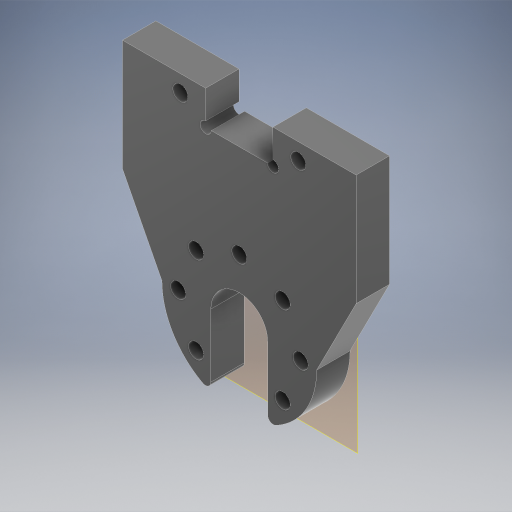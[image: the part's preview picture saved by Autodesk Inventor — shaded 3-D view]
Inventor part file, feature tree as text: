
AUTODESK INVENTOR PART (.ipt)
format: ipt  version: 2024 (Build 280153000, 153)  size: 315,904 bytes
history: native  units: in
note: dims shown in document units (in); Inventor stores cm internally (conversion verified against a paired STEP export)
features: other x3, extrude x2, sketch x2, fillet x1, reference x1
ambient origin geometry x8: Origin, YZ Plane, XZ Plane, XY Plane, X Axis, Y Axis, Z Axis, Center Point
bodies: Body1 (feature_tree)
feature tree (9):
  other  "작업 평면1"
  extrude  "돌출8"  Depth=0.1063in
  fillet  "모깎기2"  Radius=3.1496in
  extrude  "돌출9"  Depth=0.0039in
  sketch  "스케치1"
  reference  "참조1"
  sketch  "스케치3"
  other  "조립품11"
  other  "64-106Horn:1"
